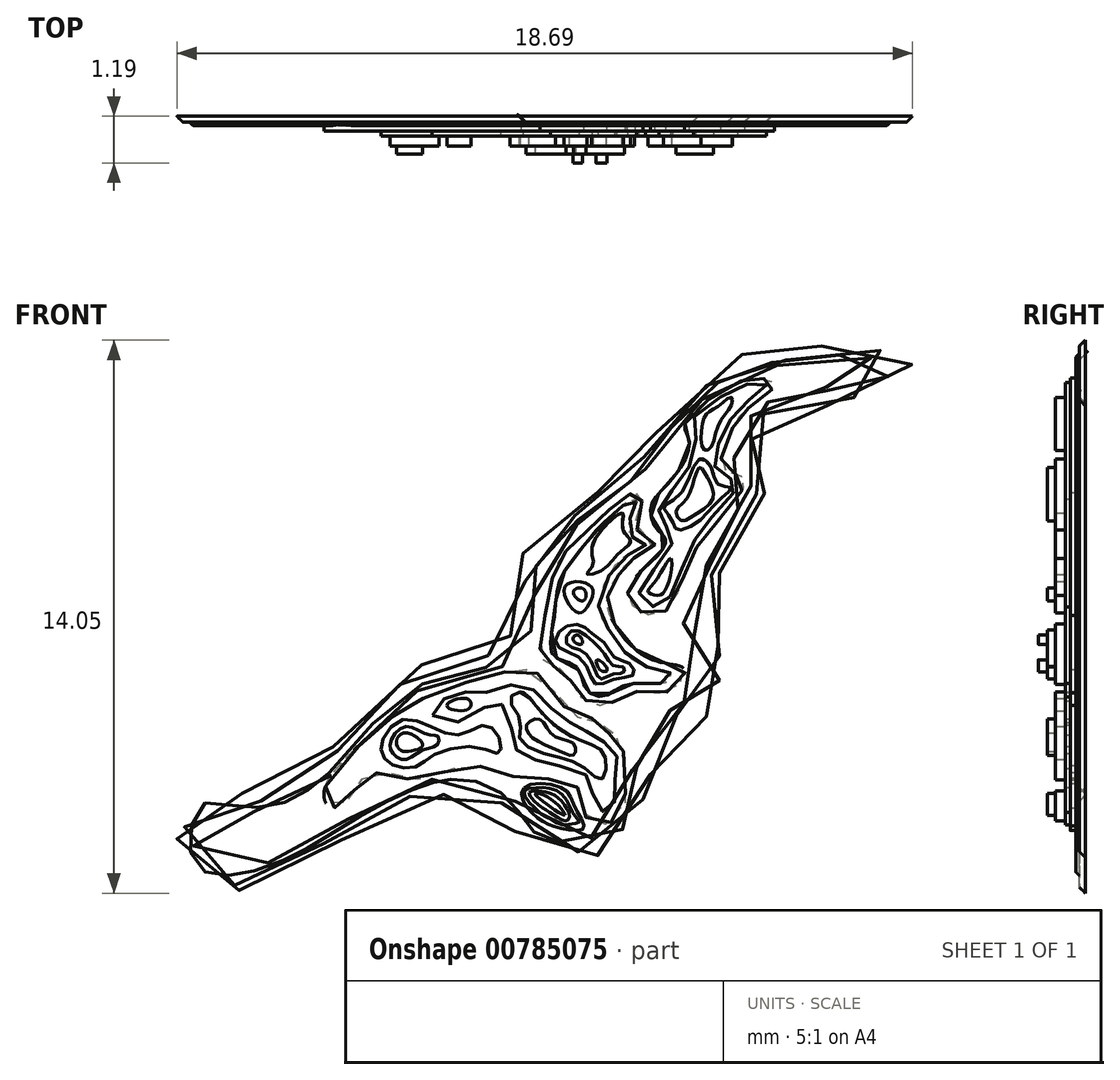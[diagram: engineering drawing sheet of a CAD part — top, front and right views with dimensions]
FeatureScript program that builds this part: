
annotation { "Feature Type Name" : "Feature", "Feature Type Description" : "" }
export const myFeature = defineFeature(function(context is Context, id is Id, definition is map)
    precondition{}
    {
        {
            var Q0;
            Q0=qCreatedBy(makeId("Front.planeOp"),FACE);
            var sketch = newSketch(context, id + "F0", { "sketchPlane" : qUnion([Q0])});
            skFitSpline(sketch, "E0", {"points": [v(-44.38, 22.55) * mm, v(-42.28, 24.57) * mm, v(-40.27, 25.1) * mm, v(-39.65, 25.88) * mm, v(-39.56, 27.46) * mm, v(-38.25, 28.6) * mm, v(-36.85, 29.74) * mm, v(-35.97, 30.8) * mm, v(-33.96, 32.55) * mm, v(-32.64, 32.55) * mm, v(-31.24, 32.9) * mm, v(-29.66, 32.2) * mm, v(-31.41, 31.23) * mm, v(-32.82, 31.23) * mm, v(-33.78, 30.1) * mm, v(-33.25, 29.48) * mm, v(-33.78, 28.51) * mm, v(-34.48, 27.11) * mm, v(-35.1, 25.7) * mm, v(-34.3, 24.75) * mm, v(-34.66, 23.43) * mm, v(-36.06, 23) * mm, v(-36.5, 20.63) * mm, v(-38.07, 19.75) * mm, v(-39.56, 20.19) * mm, v(-40.35, 21.15) * mm, v(-42.1, 21.24) * mm, v(-44.47, 20.01) * mm, v(-46.58, 18.96) * mm, v(-48.15, 19.22) * mm, v(-47.89, 21.42) * mm, v(-46.31, 21.33) * mm, v(-44.38, 22.55) * mm]});
            skFitSpline(sketch, "E1", {"points": [v(-32.16, 32.42) * mm, v(-31.12, 32.56) * mm, v(-30.32, 32.36) * mm, v(-30.26, 31.99) * mm, v(-31.33, 31.58) * mm, v(-32.82, 31.61) * mm, v(-33.72, 30.86) * mm, v(-34.18, 29.88) * mm, v(-33.6, 29.45) * mm, v(-34.2, 28.41) * mm, v(-34.9, 26.97) * mm, v(-35.53, 25.9) * mm, v(-34.73, 24.72) * mm, v(-34.7, 23.74) * mm, v(-35.97, 23.4) * mm, v(-36.74, 21.44) * mm, v(-36.92, 20.54) * mm, v(-38.07, 20.11) * mm, v(-39.25, 20.37) * mm, v(-39.89, 21.18) * mm, v(-41.1, 21.73) * mm, v(-42.6, 21.35) * mm, v(-44.1, 20.54) * mm, v(-45.42, 19.77) * mm, v(-47.12, 19.27) * mm, v(-47.9, 19.6) * mm, v(-47.99, 20.57) * mm, v(-47.61, 21.15) * mm, v(-46.6, 21.03) * mm, v(-45.16, 21.38) * mm, v(-43.98, 22.47) * mm, v(-42.94, 23.6) * mm, v(-42.02, 24.2) * mm, v(-40.95, 24.5) * mm, v(-39.63, 24.95) * mm, v(-39.34, 25.88) * mm, v(-39.28, 27.03) * mm, v(-38.39, 28.18) * mm, v(-37.12, 29.05) * mm, v(-36.25, 30.06) * mm, v(-35.33, 31.23) * mm, v(-34.3, 32.02) * mm, v(-33.49, 32.3) * mm, v(-32.16, 32.42) * mm]});
            skFitSpline(sketch, "E2", {"points": [v(-35.45, 30.78) * mm, v(-34.27, 31.73) * mm, v(-33.54, 31.93) * mm, v(-33.17, 31.76) * mm, v(-33.76, 31.23) * mm, v(-34.27, 30.6) * mm, v(-34.46, 29.63) * mm, v(-33.93, 29.37) * mm, v(-34.58, 28.33) * mm, v(-35.33, 27.27) * mm, v(-35.98, 25.98) * mm, v(-36.68, 26.06) * mm, v(-36.88, 26.6) * mm, v(-36.2, 27.35) * mm, v(-35.92, 27.83) * mm, v(-36.18, 28.1) * mm, v(-36.3, 28.7) * mm, v(-35.76, 29.37) * mm, v(-35.33, 30.3) * mm, v(-35.45, 30.78) * mm]});
            skFitSpline(sketch, "E3", {"points": [v(-36.74, 27.35) * mm, v(-36.2, 27.72) * mm, v(-36.68, 28.1) * mm, v(-36.51, 28.95) * mm, v(-36.85, 28.98) * mm, v(-37.44, 28.5) * mm, v(-38.2, 27.8) * mm, v(-38.73, 27.1) * mm, v(-39.04, 25.58) * mm, v(-39.04, 24.77) * mm, v(-38.48, 24.46) * mm, v(-38.2, 23.95) * mm, v(-37.5, 23.62) * mm, v(-36.77, 23.95) * mm, v(-35.81, 23.98) * mm, v(-35.45, 24.51) * mm, v(-36.18, 24.74) * mm, v(-37.12, 25.5) * mm, v(-37.41, 26.34) * mm, v(-37.12, 26.93) * mm, v(-36.74, 27.35) * mm]});
            skFitSpline(sketch, "E4", {"points": [v(-44.58, 21.56) * mm, v(-43.16, 23.07) * mm, v(-42.45, 23.62) * mm, v(-41.1, 24.17) * mm, v(-39.89, 24.5) * mm, v(-39.11, 24.37) * mm, v(-38.26, 23.36) * mm, v(-37.7, 23.26) * mm, v(-37.41, 22.93) * mm, v(-37.12, 22.8) * mm, v(-36.97, 21.73) * mm, v(-37.12, 20.77) * mm, v(-37.86, 20.6) * mm, v(-38.02, 21.18) * mm, v(-38.42, 21.73) * mm, v(-39.33, 21.73) * mm, v(-40.24, 21.96) * mm, v(-41.1, 22.06) * mm, v(-42.25, 21.73) * mm, v(-43.04, 21.9) * mm, v(-43.66, 21.73) * mm, v(-44.03, 21.18) * mm, v(-44.45, 21.03) * mm, v(-44.58, 21.56) * mm]});
            skFitSpline(sketch, "E5", {"points": [v(-39.54, 21.52) * mm, v(-38.56, 21.52) * mm, v(-38.24, 21.03) * mm, v(-38.02, 20.48) * mm, v(-38.56, 20.48) * mm, v(-39.01, 20.65) * mm, v(-39.46, 21.03) * mm, v(-39.54, 21.52) * mm]});
            skFitSpline(sketch, "E6", {"points": [v(-39.54, 21.44) * mm, v(-39.27, 21.52) * mm, v(-38.92, 21.52) * mm, v(-38.6, 21.38) * mm, v(-38.4, 21.1) * mm, v(-38.24, 20.8) * mm, v(-38.13, 20.64) * mm, v(-38.36, 20.6) * mm, v(-38.62, 20.6) * mm, v(-38.88, 20.74) * mm, v(-39.08, 20.84) * mm, v(-39.23, 20.98) * mm, v(-39.4, 21.15) * mm, v(-39.54, 21.44) * mm]});
            skFitSpline(sketch, "E7", {"points": [v(-39.4, 21.4) * mm, v(-38.98, 21.4) * mm, v(-38.68, 21.28) * mm, v(-38.48, 21.05) * mm, v(-38.38, 20.8) * mm, v(-38.44, 20.68) * mm, v(-38.66, 20.75) * mm, v(-38.93, 20.92) * mm, v(-39.17, 21.09) * mm, v(-39.4, 21.4) * mm]});
            skFitSpline(sketch, "E8", {"points": [v(-38.5, 20.82) * mm, v(-38.89, 21.26) * mm, v(-39.24, 21.37) * mm, v(-39.02, 21.15) * mm, v(-38.5, 20.82) * mm]});
            skFitSpline(sketch, "E9", {"points": [v(-35.2, 30.95) * mm, v(-34.32, 31.56) * mm, v(-33.66, 31.82) * mm, v(-33.38, 31.75) * mm, v(-33.73, 31.44) * mm, v(-34.23, 30.95) * mm, v(-34.57, 30.3) * mm, v(-34.7, 29.74) * mm, v(-34.47, 29.42) * mm, v(-34.1, 29.28) * mm, v(-34.47, 28.7) * mm, v(-35.03, 28.07) * mm, v(-35.45, 27.27) * mm, v(-35.83, 26.36) * mm, v(-36.15, 26.12) * mm, v(-36.56, 26.3) * mm, v(-36.52, 26.72) * mm, v(-35.85, 27.53) * mm, v(-35.79, 28.03) * mm, v(-35.98, 28.2) * mm, v(-36.1, 28.56) * mm, v(-35.82, 29.01) * mm, v(-35.33, 29.68) * mm, v(-35.17, 30.45) * mm, v(-35.2, 30.95) * mm]});
            skFitSpline(sketch, "E10", {"points": [v(-35, 30.78) * mm, v(-34.85, 31.06) * mm, v(-34.58, 31.23) * mm, v(-34.27, 31.44) * mm, v(-34.27, 31.23) * mm, v(-34.58, 30.78) * mm, v(-34.79, 30.16) * mm, v(-34.97, 30.12) * mm, v(-35, 30.78) * mm]});
            skFitSpline(sketch, "E11", {"points": [v(-35.09, 29.86) * mm, v(-35.58, 28.95) * mm, v(-35.98, 28.66) * mm, v(-35.77, 28.33) * mm, v(-35.64, 28.07) * mm, v(-35.04, 28.33) * mm, v(-34.57, 28.83) * mm, v(-34.27, 29.15) * mm, v(-34.57, 29.2) * mm, v(-34.79, 29.68) * mm, v(-35.09, 29.86) * mm]});
            skFitSpline(sketch, "E12", {"points": [v(-35.2, 29.39) * mm, v(-35.06, 29.66) * mm, v(-34.92, 29.5) * mm, v(-34.77, 29.2) * mm, v(-34.74, 28.83) * mm, v(-35.24, 28.42) * mm, v(-35.54, 28.31) * mm, v(-35.67, 28.56) * mm, v(-35.42, 28.83) * mm, v(-35.2, 29.39) * mm]});
            skFitSpline(sketch, "E13", {"points": [v(-35.8, 27.34) * mm, v(-36.23, 26.72) * mm, v(-36.38, 26.5) * mm, v(-36.14, 26.4) * mm, v(-35.88, 26.68) * mm, v(-35.8, 27.34) * mm]});
            skFitSpline(sketch, "E14", {"points": [v(-37.5, 28.26) * mm, v(-37.02, 28.7) * mm, v(-36.73, 28.86) * mm, v(-36.68, 28.7) * mm, v(-36.83, 28.38) * mm, v(-36.86, 28) * mm, v(-36.58, 27.77) * mm, v(-36.44, 27.7) * mm, v(-36.72, 27.53) * mm, v(-37.2, 27.17) * mm, v(-37.63, 26.2) * mm, v(-37.45, 25.65) * mm, v(-36.97, 24.97) * mm, v(-36.4, 24.59) * mm, v(-35.82, 24.45) * mm, v(-35.87, 24.23) * mm, v(-36.28, 24.17) * mm, v(-37.05, 24.1) * mm, v(-37.5, 23.84) * mm, v(-37.95, 24.02) * mm, v(-38.21, 24.6) * mm, v(-38.8, 24.9) * mm, v(-38.77, 25.78) * mm, v(-38.64, 26.72) * mm, v(-38.11, 27.55) * mm, v(-37.5, 28.26) * mm]});
            skFitSpline(sketch, "E15", {"points": [v(-38.64, 25.48) * mm, v(-38.67, 25.1) * mm, v(-38.05, 24.77) * mm, v(-37.72, 24.16) * mm, v(-37.23, 24.28) * mm, v(-36.74, 24.4) * mm, v(-36.83, 24.66) * mm, v(-37.21, 24.82) * mm, v(-37.48, 25.2) * mm, v(-37.76, 25.4) * mm, v(-38.13, 25.67) * mm, v(-38.64, 25.48) * mm]});
            skFitSpline(sketch, "E16", {"points": [v(-37.8, 27.63) * mm, v(-37.15, 28.45) * mm, v(-37.01, 28.48) * mm, v(-37.02, 28.08) * mm, v(-36.82, 27.78) * mm, v(-37.14, 27.46) * mm, v(-37.54, 27.05) * mm, v(-37.94, 26.96) * mm, v(-37.77, 27.19) * mm, v(-37.8, 27.63) * mm]});
            skFitSpline(sketch, "E17", {"points": [v(-38.5, 26.63) * mm, v(-37.86, 26.67) * mm, v(-37.83, 26.27) * mm, v(-38.16, 25.97) * mm, v(-38.5, 26.63) * mm]});
            skFitSpline(sketch, "E18", {"points": [v(-38.28, 26.5) * mm, v(-38.01, 26.56) * mm, v(-38.02, 26.27) * mm, v(-38.28, 26.5) * mm]});
            skFitSpline(sketch, "E19", {"points": [v(-38.45, 25.18) * mm, v(-38.32, 25.51) * mm, v(-37.83, 25.29) * mm, v(-37.47, 24.88) * mm, v(-37.23, 24.6) * mm, v(-37.01, 24.59) * mm, v(-37, 24.45) * mm, v(-37.3, 24.4) * mm, v(-37.58, 24.28) * mm, v(-37.76, 24.58) * mm, v(-38.05, 25) * mm, v(-38.45, 25.18) * mm]});
            skFitSpline(sketch, "E20", {"points": [v(-38.05, 25.18) * mm, v(-38.28, 25.26) * mm, v(-38.18, 25.4) * mm, v(-38.05, 25.18) * mm]});
            skFitSpline(sketch, "E21", {"points": [v(-37.68, 24.77) * mm, v(-37.58, 24.5) * mm, v(-37.42, 24.52) * mm, v(-37.68, 24.77) * mm]});
            skFitSpline(sketch, "E22", {"points": [v(-42.6, 23.26) * mm, v(-43.13, 22.72) * mm, v(-43.12, 22.33) * mm, v(-42.79, 22.06) * mm, v(-42.24, 22.06) * mm, v(-41.82, 22.36) * mm, v(-40.65, 22.54) * mm, v(-40.15, 22.4) * mm, v(-40.17, 22.78) * mm, v(-40.51, 23.11) * mm, v(-41.1, 22.88) * mm, v(-41.76, 23) * mm, v(-42.6, 23.26) * mm]});
            skFitSpline(sketch, "E23", {"points": [v(-41.85, 23.36) * mm, v(-40.95, 23.26) * mm, v(-40.27, 23.73) * mm, v(-39.89, 23.26) * mm, v(-39.76, 22.54) * mm, v(-39.3, 22.25) * mm, v(-38.6, 22.06) * mm, v(-37.83, 21.73) * mm, v(-37.76, 21.18) * mm, v(-37.42, 20.9) * mm, v(-37.21, 21.24) * mm, v(-37.21, 21.86) * mm, v(-37.21, 22.48) * mm, v(-37.7, 22.78) * mm, v(-38.05, 23.02) * mm, v(-38.5, 23.26) * mm, v(-39.04, 23.76) * mm, v(-39.63, 24.16) * mm, v(-40.44, 23.95) * mm, v(-40.95, 23.95) * mm, v(-41.58, 23.77) * mm, v(-41.85, 23.36) * mm]});
            skFitSpline(sketch, "E24", {"points": [v(-41.5, 23.6) * mm, v(-40.95, 23.77) * mm, v(-40.95, 23.52) * mm, v(-41.5, 23.6) * mm]});
            skFitSpline(sketch, "E25", {"points": [v(-39.63, 23.95) * mm, v(-39.89, 23.76) * mm, v(-39.63, 23.26) * mm, v(-39.63, 22.75) * mm, v(-38.8, 22.33) * mm, v(-38.05, 22.06) * mm, v(-37.58, 21.73) * mm, v(-37.44, 22.06) * mm, v(-37.58, 22.5) * mm, v(-38.05, 22.7) * mm, v(-38.63, 23.02) * mm, v(-39.16, 23.52) * mm, v(-39.63, 23.95) * mm]});
            skFitSpline(sketch, "E26", {"points": [v(-39.13, 23.26) * mm, v(-39.46, 23.13) * mm, v(-39.34, 22.8) * mm, v(-38.61, 22.45) * mm, v(-38.26, 22.36) * mm, v(-38.26, 22.63) * mm, v(-38.8, 22.85) * mm, v(-39.13, 23.26) * mm]});
            skFitSpline(sketch, "E27", {"points": [v(-42.53, 23.07) * mm, v(-42.92, 22.69) * mm, v(-42.86, 22.39) * mm, v(-42.55, 22.24) * mm, v(-42.1, 22.48) * mm, v(-41.73, 22.61) * mm, v(-41.72, 22.82) * mm, v(-41.97, 22.87) * mm, v(-42.53, 23.07) * mm]});
            skFitSpline(sketch, "E28", {"points": [v(-42.5, 22.91) * mm, v(-42.77, 22.73) * mm, v(-42.67, 22.47) * mm, v(-42.4, 22.45) * mm, v(-42.1, 22.6) * mm, v(-42.5, 22.91) * mm]});
            skSolve(sketch);
        }
        {
            var Q0;
            Q0=makeQuery(id+"F0.imprint","IMPRINT",FACE,{"disambiguationData":[TD([[makeQuery(id+"F0.imprint","IMPRINT",EDGE,{"derivedFrom":sQuery(id+"F0.wireOp",EDGE,"E0")}),-1.0]])]});
            extrude(context, id + "F1", {"entities" : qUnion([Q0]), "depth" : 0.15 * mm, "offsetDistance" : 25.4 * mm});
        }
        {
            var Q0;
            Q0=makeQuery(id+"F0.imprint","IMPRINT",FACE,{"disambiguationData":[TD([[makeQuery(id+"F0.imprint","IMPRINT",EDGE,{"derivedFrom":sQuery(id+"F0.wireOp",EDGE,"E1")}),-1.0]])]});
            extrude(context, id + "F2", {"entities" : qUnion([Q0]), "operationType" : NewBodyOperationType.ADD, "depth" : 0.24 * mm, "offsetDistance" : 25.4 * mm});
        }
        {
            var Q0;
            Q0=makeQuery(id+"F0.imprint","IMPRINT",FACE,{"disambiguationData":[TD([[makeQuery(id+"F0.imprint","IMPRINT",EDGE,{"derivedFrom":sQuery(id+"F0.wireOp",EDGE,"E4")}),-1.0]])]});
            var Q1;
            Q1=makeQuery(id+"F0.imprint","IMPRINT",FACE,{"disambiguationData":[TD([[makeQuery(id+"F0.imprint","IMPRINT",EDGE,{"derivedFrom":sQuery(id+"F0.wireOp",EDGE,"E3")}),1.0]])]});
            var Q2;
            Q2=makeQuery(id+"F0.imprint","IMPRINT",FACE,{"disambiguationData":[TD([[makeQuery(id+"F0.imprint","IMPRINT",EDGE,{"derivedFrom":sQuery(id+"F0.wireOp",EDGE,"E2")}),-1.0]])]});
            var Q3;
            Q3=makeQuery(id+"F0.imprint","IMPRINT",FACE,{"disambiguationData":[TD([[makeQuery(id+"F0.imprint","IMPRINT",EDGE,{"derivedFrom":sQuery(id+"F0.wireOp",EDGE,"E5")}),-1.0]])]});
            extrude(context, id + "F3", {"entities" : qUnion([Q0, Q1, Q2, Q3]), "operationType" : NewBodyOperationType.ADD, "depth" : 0.38 * mm, "offsetDistance" : 25.4 * mm});
        }
        {
            var Q0;
            Q0=makeQuery(id+"F0.imprint","IMPRINT",FACE,{"disambiguationData":[TD([[makeQuery(id+"F0.imprint","IMPRINT",EDGE,{"derivedFrom":sQuery(id+"F0.wireOp",EDGE,"E22")}),1.0]])]});
            var Q1;
            Q1=makeQuery(id+"F0.imprint","IMPRINT",FACE,{"disambiguationData":[TD([[makeQuery(id+"F0.imprint","IMPRINT",EDGE,{"derivedFrom":sQuery(id+"F0.wireOp",EDGE,"E23")}),1.0]])]});
            var Q2;
            Q2=makeQuery(id+"F0.imprint","IMPRINT",FACE,{"disambiguationData":[TD([[makeQuery(id+"F0.imprint","IMPRINT",EDGE,{"derivedFrom":sQuery(id+"F0.wireOp",EDGE,"E14")}),-1.0]])]});
            var Q3;
            Q3=makeQuery(id+"F0.imprint","IMPRINT",FACE,{"disambiguationData":[TD([[makeQuery(id+"F0.imprint","IMPRINT",EDGE,{"derivedFrom":sQuery(id+"F0.wireOp",EDGE,"E6")}),-1.0]])]});
            var Q4;
            Q4=makeQuery(id+"F0.imprint","IMPRINT",FACE,{"disambiguationData":[TD([[makeQuery(id+"F0.imprint","IMPRINT",EDGE,{"derivedFrom":sQuery(id+"F0.wireOp",EDGE,"E9")}),-1.0]])]});
            extrude(context, id + "F4", {"entities" : qUnion([Q0, Q1, Q2, Q3, Q4]), "operationType" : NewBodyOperationType.ADD, "depth" : 0.5 * mm, "offsetDistance" : 25.4 * mm});
        }
        {
            var Q0;
            Q0=makeQuery(id+"F0.imprint","IMPRINT",FACE,{"disambiguationData":[TD([[makeQuery(id+"F0.imprint","IMPRINT",EDGE,{"derivedFrom":sQuery(id+"F0.wireOp",EDGE,"E16")}),-1.0]])]});
            var Q1;
            Q1=makeQuery(id+"F0.imprint","IMPRINT",FACE,{"disambiguationData":[TD([[makeQuery(id+"F0.imprint","IMPRINT",EDGE,{"derivedFrom":sQuery(id+"F0.wireOp",EDGE,"E17")}),-1.0]])]});
            var Q2;
            Q2=makeQuery(id+"F0.imprint","IMPRINT",FACE,{"disambiguationData":[TD([[makeQuery(id+"F0.imprint","IMPRINT",EDGE,{"derivedFrom":sQuery(id+"F0.wireOp",EDGE,"E15")}),1.0]])]});
            var Q3;
            Q3=makeQuery(id+"F0.imprint","IMPRINT",FACE,{"disambiguationData":[TD([[makeQuery(id+"F0.imprint","IMPRINT",EDGE,{"derivedFrom":sQuery(id+"F0.wireOp",EDGE,"E11")}),1.0]])]});
            var Q4;
            Q4=makeQuery(id+"F0.imprint","IMPRINT",FACE,{"disambiguationData":[TD([[makeQuery(id+"F0.imprint","IMPRINT",EDGE,{"derivedFrom":sQuery(id+"F0.wireOp",EDGE,"E10")}),-1.0]])]});
            var Q5;
            Q5=makeQuery(id+"F0.imprint","IMPRINT",FACE,{"disambiguationData":[TD([[makeQuery(id+"F0.imprint","IMPRINT",EDGE,{"derivedFrom":sQuery(id+"F0.wireOp",EDGE,"E13")}),1.0]])]});
            var Q6;
            Q6=makeQuery(id+"F0.imprint","IMPRINT",FACE,{"disambiguationData":[TD([[makeQuery(id+"F0.imprint","IMPRINT",EDGE,{"derivedFrom":sQuery(id+"F0.wireOp",EDGE,"E25")}),1.0]])]});
            var Q7;
            Q7=makeQuery(id+"F0.imprint","IMPRINT",FACE,{"disambiguationData":[TD([[makeQuery(id+"F0.imprint","IMPRINT",EDGE,{"derivedFrom":sQuery(id+"F0.wireOp",EDGE,"E24")}),-1.0]])]});
            var Q8;
            Q8=makeQuery(id+"F0.imprint","IMPRINT",FACE,{"disambiguationData":[TD([[makeQuery(id+"F0.imprint","IMPRINT",EDGE,{"derivedFrom":sQuery(id+"F0.wireOp",EDGE,"E27")}),1.0]])]});
            var Q9;
            Q9=makeQuery(id+"F0.imprint","IMPRINT",FACE,{"disambiguationData":[TD([[makeQuery(id+"F0.imprint","IMPRINT",EDGE,{"derivedFrom":sQuery(id+"F0.wireOp",EDGE,"E7")}),-1.0]])]});
            extrude(context, id + "F5", {"entities" : qUnion([Q0, Q1, Q2, Q3, Q4, Q5, Q6, Q7, Q8, Q9]), "operationType" : NewBodyOperationType.ADD, "depth" : 0.76 * mm, "offsetDistance" : 25.4 * mm});
        }
        {
            var Q0;
            Q0=makeQuery(id+"F0.imprint","IMPRINT",FACE,{"disambiguationData":[TD([[makeQuery(id+"F0.imprint","IMPRINT",EDGE,{"derivedFrom":sQuery(id+"F0.wireOp",EDGE,"E12")}),-1.0]])]});
            var Q1;
            Q1=makeQuery(id+"F0.imprint","IMPRINT",FACE,{"disambiguationData":[TD([[makeQuery(id+"F0.imprint","IMPRINT",EDGE,{"derivedFrom":sQuery(id+"F0.wireOp",EDGE,"E18")}),-1.0]])]});
            var Q2;
            Q2=makeQuery(id+"F0.imprint","IMPRINT",FACE,{"disambiguationData":[TD([[makeQuery(id+"F0.imprint","IMPRINT",EDGE,{"derivedFrom":sQuery(id+"F0.wireOp",EDGE,"E19")}),-1.0]])]});
            var Q3;
            Q3=makeQuery(id+"F0.imprint","IMPRINT",FACE,{"disambiguationData":[TD([[makeQuery(id+"F0.imprint","IMPRINT",EDGE,{"derivedFrom":sQuery(id+"F0.wireOp",EDGE,"E26")}),1.0]])]});
            var Q4;
            Q4=makeQuery(id+"F0.imprint","IMPRINT",FACE,{"disambiguationData":[TD([[makeQuery(id+"F0.imprint","IMPRINT",EDGE,{"derivedFrom":sQuery(id+"F0.wireOp",EDGE,"E28")}),1.0]])]});
            var Q5;
            Q5=makeQuery(id+"F0.imprint","IMPRINT",FACE,{"disambiguationData":[TD([[makeQuery(id+"F0.imprint","IMPRINT",EDGE,{"derivedFrom":sQuery(id+"F0.wireOp",EDGE,"E8")}),1.0]])]});
            extrude(context, id + "F6", {"entities" : qUnion([Q0, Q1, Q2, Q3, Q4, Q5]), "operationType" : NewBodyOperationType.ADD, "depth" : 0.97 * mm, "offsetDistance" : 25.4 * mm});
        }
        {
            var Q0;
            Q0=makeQuery(id+"F0.imprint","IMPRINT",FACE,{"disambiguationData":[TD([[makeQuery(id+"F0.imprint","IMPRINT",EDGE,{"derivedFrom":sQuery(id+"F0.wireOp",EDGE,"E21")}),1.0]])]});
            var Q1;
            Q1=makeQuery(id+"F0.imprint","IMPRINT",FACE,{"disambiguationData":[TD([[makeQuery(id+"F0.imprint","IMPRINT",EDGE,{"derivedFrom":sQuery(id+"F0.wireOp",EDGE,"E20")}),-1.0]])]});
            extrude(context, id + "F7", {"entities" : qUnion([Q0, Q1]), "operationType" : NewBodyOperationType.ADD, "depth" : 1.2 * mm, "offsetDistance" : 25.4 * mm});
        }
        {
            var Q0;
            Q0=makeQuery(id+"F1.opExtrude","CAP_EDGE",EDGE,{"disambiguationData":[OSD([sQuery(id+"F0.wireOp",EDGE,"E0")])],"isStart":false});
            chamfer(context, id + "F8", {"entities" : qUnion([Q0]), "width" : 0.15 * mm, "tangentPropagation" : true});
        }
        {
            var Q0;
            Q0=makeQuery(id+"F2.opExtrude","CAP_EDGE",EDGE,{"disambiguationData":[OSD([sQuery(id+"F0.wireOp",EDGE,"E1")])],"isStart":false});
            chamfer(context, id + "F9", {"entities" : qUnion([Q0]), "width" : 0.1 * mm, "tangentPropagation" : true});
        }
    });
